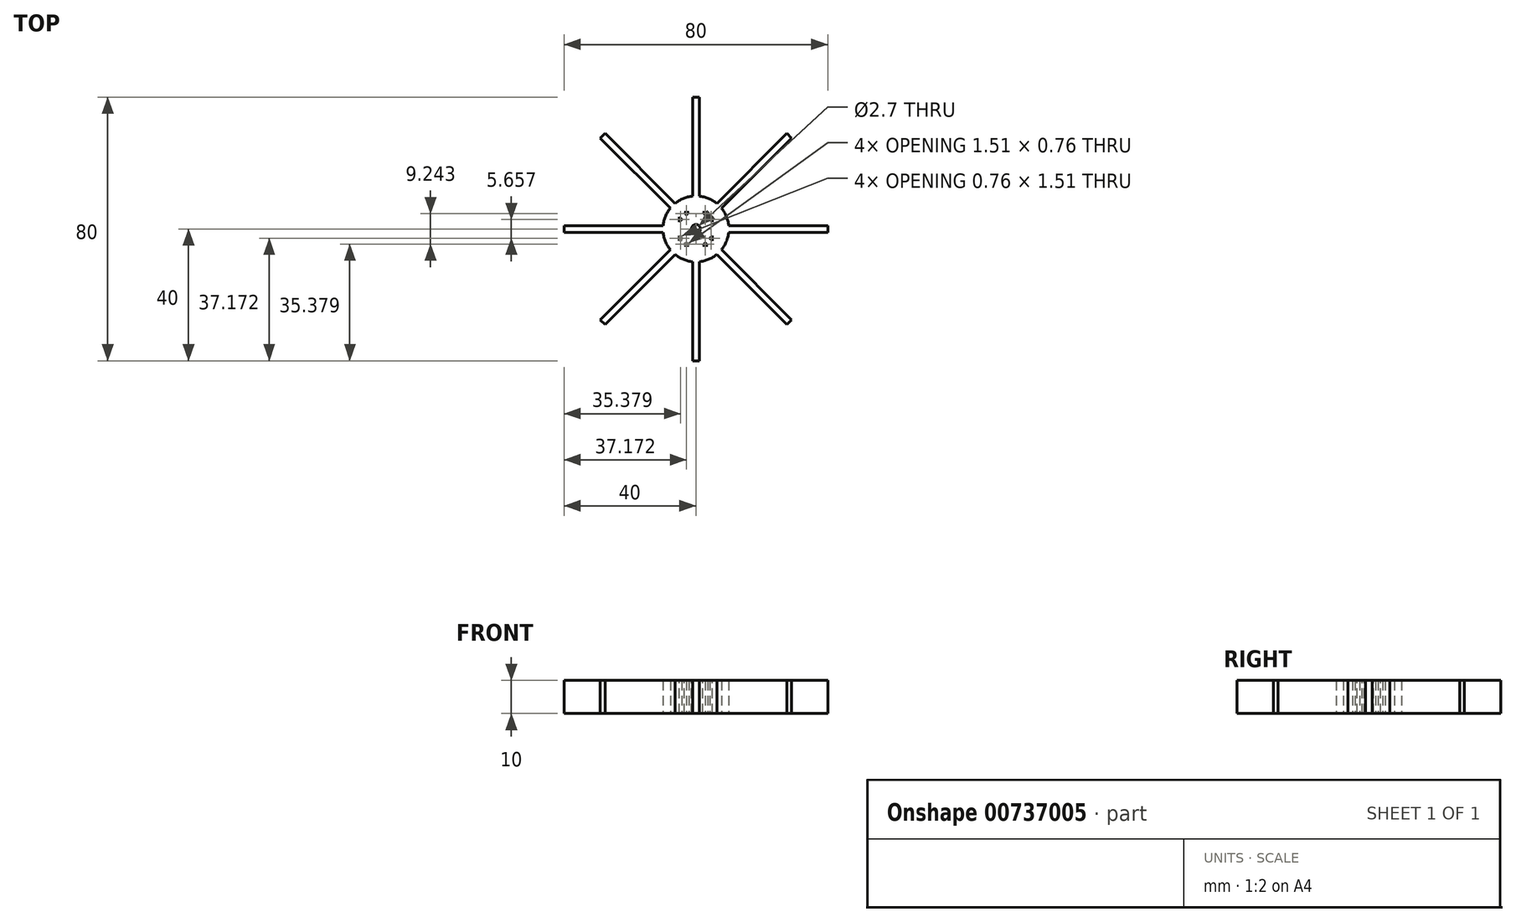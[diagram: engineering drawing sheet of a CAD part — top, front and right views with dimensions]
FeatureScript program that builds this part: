
annotation { "Feature Type Name" : "Feature", "Feature Type Description" : "" }
export const myFeature = defineFeature(function(context is Context, id is Id, definition is map)
    precondition{}
    {
        {
            assignVariable(context, id + "F0", {"name" : "size", "anyValue" : 10});
        }
        {
            var Q0;
            Q0=qCreatedBy(makeId("Top.planeOp"),FACE);
            var sketch = newSketch(context, id + "F1", { "sketchPlane" : qUnion([Q0])});
            skCircle(sketch, "E0", {"center": v(0, 0) * mm, "radius": 10 * mm});
            skLineSegment(sketch, "E1.bottom", {"start": v(-5, 5) * mm, "end": v(5, 5) * mm});
            skLineSegment(sketch, "E1.top", {"start": v(-5, -5) * mm, "end": v(5, -5) * mm});
            skLineSegment(sketch, "E1.left", {"start": v(-5, 5) * mm, "end": v(-5, -5) * mm});
            skLineSegment(sketch, "E1.right", {"start": v(5, 5) * mm, "end": v(5, -5) * mm});
            skLineSegment(sketch, "E2", {"start": v(0, 5) * mm, "end": v(0, 0) * mm});
            skLineSegment(sketch, "E3", {"start": v(5, 0) * mm, "end": v(0, 0) * mm});
            skLineSegment(sketch, "E4.top", {"start": v(5, -1) * mm, "end": v(40, -1) * mm});
            skLineSegment(sketch, "E4.left", {"start": v(5, 1) * mm, "end": v(5, -1) * mm});
            skLineSegment(sketch, "E4.right", {"start": v(40, 1) * mm, "end": v(40, -1) * mm});
            skLineSegment(sketch, "E5", {"start": v(5, -1) * mm, "end": v(2.89, -1) * mm});
            skLineSegment(sketch, "E6", {"start": v(2.89, 0) * mm, "end": v(2.89, -1) * mm});
            skLineSegment(sketch, "E7", {"start": v(5, 1) * mm, "end": v(2.14, 1) * mm});
            skLineSegment(sketch, "E8", {"start": v(2.14, 1) * mm, "end": v(2.14, 0) * mm});
            skLineSegment(sketch, "E9", {"start": v(-5, -5) * mm, "end": v(5, 5) * mm});
            skLineSegment(sketch, "E10.MirrorCS", {"start": v(1, 5) * mm, "end": v(1, 40) * mm});
            skLineSegment(sketch, "E11.MirrorCS", {"start": v(-1, 5) * mm, "end": v(-1, 40) * mm});
            skLineSegment(sketch, "E12.MirrorCS", {"start": v(1, 40) * mm, "end": v(-1, 40) * mm});
            skLineSegment(sketch, "E13.MirrorCS", {"start": v(-5, 1) * mm, "end": v(-40, 1) * mm});
            skLineSegment(sketch, "E14.MirrorCS", {"start": v(-5, -1) * mm, "end": v(-40, -1) * mm});
            skLineSegment(sketch, "E15.MirrorCS", {"start": v(-40, 1) * mm, "end": v(-40, -1) * mm});
            skLineSegment(sketch, "E16", {"start": v(-5, 5) * mm, "end": v(5, -5) * mm});
            skLineSegment(sketch, "E17", {"start": v(-5, 0) * mm, "end": v(5, 0) * mm});
            skLineSegment(sketch, "E18.MirrorCS", {"start": v(1, -5) * mm, "end": v(1, -40) * mm});
            skLineSegment(sketch, "E19.MirrorCS", {"start": v(-1, -5) * mm, "end": v(-1, -40) * mm});
            skLineSegment(sketch, "E20.MirrorCS", {"start": v(1, -40) * mm, "end": v(-1, -40) * mm});
            skLineSegment(sketch, "E21", {"start": v(5, 1) * mm, "end": v(40, 1) * mm});
            skSolve(sketch);
        }
        {
            var Q0;
            Q0=qCreatedBy(makeId("Top.planeOp"),FACE);
            var sketch = newSketch(context, id + "F2", { "sketchPlane" : qUnion([Q0])});
            skLineSegment(sketch, "E22", {"start": v(-4.24, 2.83) * mm, "end": v(-29, 27.58) * mm});
            skLineSegment(sketch, "E23", {"start": v(-29, 27.58) * mm, "end": v(-27.58, 29) * mm});
            skLineSegment(sketch, "E24", {"start": v(-27.58, 29) * mm, "end": v(-2.83, 4.24) * mm});
            skLineSegment(sketch, "E25", {"start": v(-7.07, 0) * mm, "end": v(0, 7.07) * mm});
            skLineSegment(sketch, "E26", {"start": v(0, 7.07) * mm, "end": v(7.07, 0) * mm});
            skLineSegment(sketch, "E27", {"start": v(7.07, 0) * mm, "end": v(0, -7.07) * mm});
            skLineSegment(sketch, "E28", {"start": v(0, -7.07) * mm, "end": v(-7.07, 0) * mm});
            skLineSegment(sketch, "E29", {"start": v(-3.54, 3.54) * mm, "end": v(3.54, -3.54) * mm});
            skLineSegment(sketch, "E30", {"start": v(-3.54, -3.54) * mm, "end": v(3.54, 3.54) * mm});
            skPoint(sketch, "E31", {"position": v(0, 0) * mm});
            skLineSegment(sketch, "E32", {"start": v(-4.24, 2.83) * mm, "end": v(-2.94, 1.53) * mm});
            skLineSegment(sketch, "E33", {"start": v(-2.94, 1.53) * mm, "end": v(-5.77, -1.3) * mm});
            skLineSegment(sketch, "E34", {"start": v(-2.83, 4.24) * mm, "end": v(-0.42, 1.84) * mm});
            skLineSegment(sketch, "E35", {"start": v(-0.42, 1.84) * mm, "end": v(2.4, 4.67) * mm});
            skLineSegment(sketch, "E36.MirrorCS", {"start": v(-4.24, -2.83) * mm, "end": v(-29, -27.58) * mm});
            skLineSegment(sketch, "E37.MirrorCS", {"start": v(-27.58, -29) * mm, "end": v(-2.83, -4.24) * mm});
            skLineSegment(sketch, "E38.MirrorCS", {"start": v(-29, -27.58) * mm, "end": v(-27.58, -29) * mm});
            skLineSegment(sketch, "E39.MirrorCS", {"start": v(2.83, -4.24) * mm, "end": v(27.58, -29) * mm});
            skLineSegment(sketch, "E40.MirrorCS", {"start": v(29, -27.58) * mm, "end": v(4.24, -2.83) * mm});
            skLineSegment(sketch, "E41.MirrorCS", {"start": v(27.58, -29) * mm, "end": v(29, -27.58) * mm});
            skLineSegment(sketch, "E42.MirrorCS", {"start": v(2.83, 4.24) * mm, "end": v(27.58, 29) * mm});
            skLineSegment(sketch, "E43.MirrorCS", {"start": v(29, 27.58) * mm, "end": v(4.24, 2.83) * mm});
            skLineSegment(sketch, "E44.MirrorCS", {"start": v(27.58, 29) * mm, "end": v(29, 27.58) * mm});
            skSolve(sketch);
        }
        {
            var Q0;
            Q0 = qSketchRegion(id + "F2", true);
            extrude(context, id + "F3", {"entities" : qUnion([Q0]), "depth" : (getVariable(context, 'size')) * mm, "offsetDistance" : 25 * mm});
        }
        {
            var Q0;
            Q0 = qSketchRegion(id + "F1", true);
            extrude(context, id + "F4", {"entities" : qUnion([Q0]), "operationType" : NewBodyOperationType.ADD, "depth" : (getVariable(context, 'size')) * mm, "offsetDistance" : 25 * mm});
        }
        {
            var Q0;
            Q0=makeQuery(id+"F4.boolean.opBoolean","MERGE",FACE,{"derivedFrom":[makeQuery(id+"F3.opExtrude","CAP_FACE",FACE,{"disambiguationData":[OSD([sQuery(id+"F2.wireOp",EDGE,"E22"),sQuery(id+"F2.wireOp",EDGE,"E23"),sQuery(id+"F2.wireOp",EDGE,"E24"),sQuery(id+"F2.wireOp",EDGE,"E25"),sQuery(id+"F2.wireOp",EDGE,"E26"),sQuery(id+"F2.wireOp",EDGE,"E27"),sQuery(id+"F2.wireOp",EDGE,"E28"),sQuery(id+"F2.wireOp",EDGE,"E36.MirrorCS"),sQuery(id+"F2.wireOp",EDGE,"E37.MirrorCS"),sQuery(id+"F2.wireOp",EDGE,"E38.MirrorCS"),sQuery(id+"F2.wireOp",EDGE,"E39.MirrorCS"),sQuery(id+"F2.wireOp",EDGE,"E40.MirrorCS"),sQuery(id+"F2.wireOp",EDGE,"E41.MirrorCS"),sQuery(id+"F2.wireOp",EDGE,"E42.MirrorCS"),sQuery(id+"F2.wireOp",EDGE,"E43.MirrorCS"),sQuery(id+"F2.wireOp",EDGE,"E44.MirrorCS")])],"isStart":false}),makeQuery(id+"F4.opExtrude","CAP_FACE",FACE,{"disambiguationData":[OSD([sQuery(id+"F1.wireOp",EDGE,"E0"),sQuery(id+"F1.wireOp",EDGE,"E1.bottom"),sQuery(id+"F1.wireOp",EDGE,"E1.top"),sQuery(id+"F1.wireOp",EDGE,"E1.left"),sQuery(id+"F1.wireOp",EDGE,"E1.right"),sQuery(id+"F1.wireOp",EDGE,"E4.top"),sQuery(id+"F1.wireOp",EDGE,"E4.left"),sQuery(id+"F1.wireOp",EDGE,"E4.right"),sQuery(id+"F1.wireOp",EDGE,"E10.MirrorCS"),sQuery(id+"F1.wireOp",EDGE,"E11.MirrorCS"),sQuery(id+"F1.wireOp",EDGE,"E12.MirrorCS"),sQuery(id+"F1.wireOp",EDGE,"E13.MirrorCS"),sQuery(id+"F1.wireOp",EDGE,"E14.MirrorCS"),sQuery(id+"F1.wireOp",EDGE,"E15.MirrorCS"),sQuery(id+"F1.wireOp",EDGE,"E18.MirrorCS"),sQuery(id+"F1.wireOp",EDGE,"E19.MirrorCS"),sQuery(id+"F1.wireOp",EDGE,"E20.MirrorCS"),sQuery(id+"F1.wireOp",EDGE,"E21")])],"isStart":false})]});
            var sketch = newSketch(context, id + "F5", { "sketchPlane" : qUnion([Q0])});
            skCircle(sketch, "E45", {"center": v(0, 0) * mm, "radius": 1.35 * mm});
            skSolve(sketch);
        }
        {
            var Q0;
            Q0 = qSketchRegion(id + "F5", true);
            extrude(context, id + "F6", {"entities" : qUnion([Q0]), "operationType" : NewBodyOperationType.REMOVE, "oppositeDirection" : true, "depth" : 25 * mm, "offsetDistance" : 25 * mm});
        }
    });
